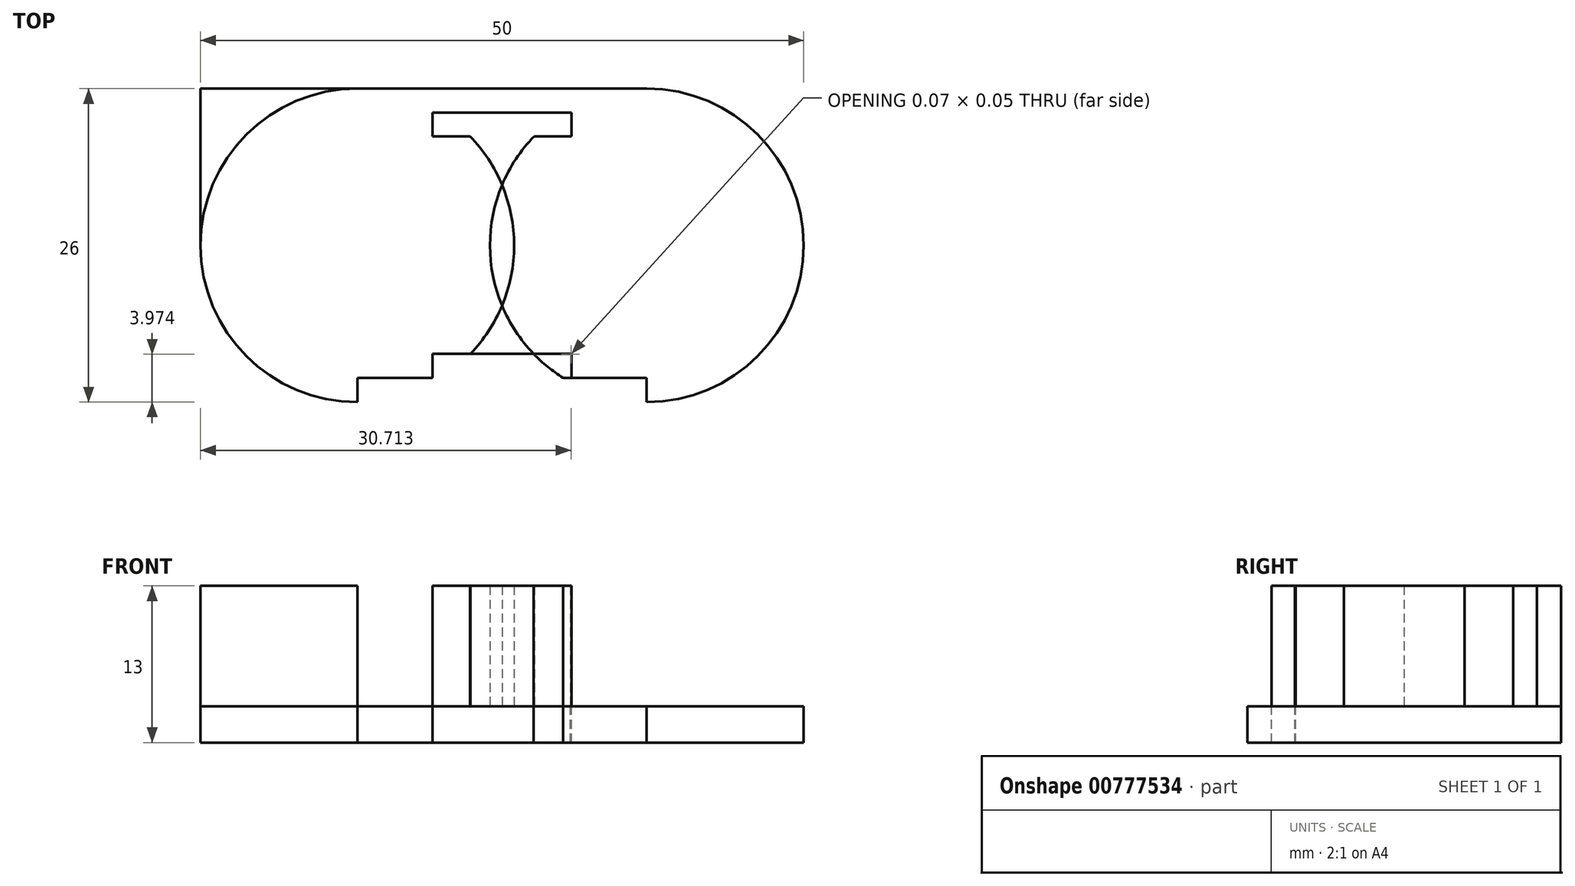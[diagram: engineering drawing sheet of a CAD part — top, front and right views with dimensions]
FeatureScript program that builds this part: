
annotation { "Feature Type Name" : "Feature", "Feature Type Description" : "" }
export const myFeature = defineFeature(function(context is Context, id is Id, definition is map)
    precondition{}
    {
        {
            var Q0;
            Q0=qCreatedBy(makeId("Top.planeOp"),FACE);
            var sketch = newSketch(context, id + "F0", { "sketchPlane" : qUnion([Q0])});
            skLineSegment(sketch, "E0.bottom", {"start": v(0, 26) * mm, "end": v(50, 26) * mm});
            skLineSegment(sketch, "E0.top", {"start": v(0, 0) * mm, "end": v(50, 0) * mm});
            skLineSegment(sketch, "E0.left", {"start": v(0, 26) * mm, "end": v(0, 0) * mm});
            skLineSegment(sketch, "E0.right", {"start": v(50, 26) * mm, "end": v(50, 0) * mm});
            skLineSegment(sketch, "E1", {"start": v(0, 13) * mm, "end": v(13, 13) * mm});
            skLineSegment(sketch, "E2", {"start": v(13, 13) * mm, "end": v(13, 0) * mm});
            skCircle(sketch, "E3", {"center": v(13, 13) * mm, "radius": 13 * mm});
            skLineSegment(sketch, "E4", {"start": v(50, 13) * mm, "end": v(37, 13) * mm});
            skLineSegment(sketch, "E5", {"start": v(37, 13) * mm, "end": v(37, 0) * mm});
            skCircle(sketch, "E6", {"center": v(37, 13) * mm, "radius": 13 * mm});
            skLineSegment(sketch, "E7", {"start": v(0, 0) * mm, "end": v(25, 0) * mm, "construction": true});
            skLineSegment(sketch, "E8.bottom", {"start": v(19.25, 0) * mm, "end": v(30.75, 0) * mm});
            skCircle(sketch, "E9", {"center": v(13, 13) * mm, "radius": 11 * mm});
            skCircle(sketch, "E10", {"center": v(37, 13) * mm, "radius": 11 * mm});
            skLineSegment(sketch, "E11", {"start": v(13, 24) * mm, "end": v(37, 24) * mm});
            skLineSegment(sketch, "E12", {"start": v(13, 13) * mm, "end": v(13, 24) * mm, "construction": true});
            skLineSegment(sketch, "E13", {"start": v(37, 13) * mm, "end": v(37, 24) * mm, "construction": true});
            skLineSegment(sketch, "E14", {"start": v(13, 2) * mm, "end": v(37, 2) * mm});
            skLineSegment(sketch, "E15.bottom", {"start": v(19.25, 2) * mm, "end": v(30.75, 2) * mm});
            skLineSegment(sketch, "E15.top", {"start": v(19.25, 4) * mm, "end": v(30.75, 4) * mm});
            skLineSegment(sketch, "E15.left", {"start": v(19.25, 2) * mm, "end": v(19.25, 4) * mm});
            skLineSegment(sketch, "E15.right", {"start": v(30.75, 2) * mm, "end": v(30.75, 4) * mm});
            skLineSegment(sketch, "E16", {"start": v(30.75, 0) * mm, "end": v(30.75, 2) * mm, "construction": true});
            skLineSegment(sketch, "E17.top", {"start": v(19.25, 24) * mm, "end": v(30.75, 24) * mm});
            skLineSegment(sketch, "E17.left", {"start": v(19.25, 2) * mm, "end": v(19.25, 24) * mm, "construction": true});
            skLineSegment(sketch, "E17.right", {"start": v(30.75, 2) * mm, "end": v(30.75, 24) * mm, "construction": true});
            skLineSegment(sketch, "E18.bottom", {"start": v(19.25, 24) * mm, "end": v(30.75, 24) * mm, "construction": true});
            skLineSegment(sketch, "E18.top", {"start": v(19.25, 22.05) * mm, "end": v(30.75, 22.05) * mm});
            skLineSegment(sketch, "E18.left", {"start": v(19.25, 24) * mm, "end": v(19.25, 22.05) * mm});
            skLineSegment(sketch, "E18.right", {"start": v(30.75, 24) * mm, "end": v(30.75, 22.05) * mm});
            skSolve(sketch);
        }
        {
            var Q0;
            {var subQ0=sQuery(id+"F0.wireOp",EDGE,"E18.top");var subQ1=sQuery(id+"F0.wireOp",EDGE,"E3");var subQ2=makeQuery(id+"F0.imprint","INTERSECT",VERTEX,{"derivedFrom":[subQ1,subQ0]});Q0=makeQuery(id+"F0.imprint","IMPRINT",FACE,{"disambiguationData":[TD([[makeQuery(id+"F0.imprint","IMPRINT",EDGE,{"disambiguationData":[TD([[subQ2,-1.0]])],"derivedFrom":subQ1}),-1.0]])]});}
            var Q1;
            {var subQ5=sQuery(id+"F0.wireOp",EDGE,"E18.left");Q1=makeQuery(id+"F0.imprint","IMPRINT",FACE,{"disambiguationData":[TD([[makeQuery(id+"F0.imprint","IMPRINT",EDGE,{"derivedFrom":subQ5}),1.0]])]});}
            var Q2;
            {var subQ5=sQuery(id+"F0.wireOp",EDGE,"E18.right");Q2=makeQuery(id+"F0.imprint","IMPRINT",FACE,{"disambiguationData":[TD([[makeQuery(id+"F0.imprint","IMPRINT",EDGE,{"derivedFrom":subQ5}),-1.0]])]});}
            var Q3;
            {var subQ0=sQuery(id+"F0.wireOp",EDGE,"E15.bottom");var subQ1=sQuery(id+"F0.wireOp",EDGE,"E3");var subQ2=makeQuery(id+"F0.imprint","INTERSECT",VERTEX,{"derivedFrom":[subQ1,subQ0]});Q3=makeQuery(id+"F0.imprint","IMPRINT",FACE,{"disambiguationData":[TD([[makeQuery(id+"F0.imprint","IMPRINT",EDGE,{"disambiguationData":[TD([[subQ2,-1.0]])],"derivedFrom":subQ1}),-1.0]])]});}
            var Q4;
            {var subQ0=sQuery(id+"F0.wireOp",EDGE,"E15.bottom");var subQ6=sQuery(id+"F0.wireOp",EDGE,"E3");var subQ9=makeQuery(id+"F0.imprint","INTERSECT",VERTEX,{"derivedFrom":[subQ6,subQ0]});Q4=makeQuery(id+"F0.imprint","IMPRINT",FACE,{"disambiguationData":[TD([[makeQuery(id+"F0.imprint","IMPRINT",EDGE,{"disambiguationData":[TD([[subQ9,-1.0]])],"derivedFrom":subQ6}),1.0]])]});}
            var Q5;
            {var subQ5=sQuery(id+"F0.wireOp",EDGE,"E15.top");var subQ6=sQuery(id+"F0.wireOp",EDGE,"E6");var subQ7=makeQuery(id+"F0.imprint","INTERSECT",VERTEX,{"derivedFrom":[subQ6,subQ5]});Q5=makeQuery(id+"F0.imprint","IMPRINT",FACE,{"disambiguationData":[TD([[makeQuery(id+"F0.imprint","IMPRINT",EDGE,{"disambiguationData":[TD([[subQ7,-1.0]])],"derivedFrom":subQ6}),1.0]])]});}
            extrude(context, id + "F1", {"entities" : qUnion([Q0, Q1, Q2, Q3, Q4, Q5]), "depth" : 10 * mm, "offsetDistance" : 25 * mm});
        }
        {
            var Q0;
            {var subQ1=sQuery(id+"F0.wireOp",EDGE,"E4");var subQ3=sQuery(id+"F0.wireOp",EDGE,"E10");var subQ4=makeQuery(id+"F0.imprint","INTERSECT",VERTEX,{"derivedFrom":[subQ1,subQ3]});Q0=makeQuery(id+"F0.imprint","IMPRINT",FACE,{"disambiguationData":[TD([[makeQuery(id+"F0.imprint","IMPRINT",EDGE,{"disambiguationData":[TD([[subQ4,1.0]])],"derivedFrom":subQ1}),1.0]])]});}
            var Q1;
            {var subQ5=sQuery(id+"F0.wireOp",EDGE,"E6");var subQ7=makeQuery(id+"F0.imprint","INTERSECT",VERTEX,{"derivedFrom":[sQuery(id+"F0.wireOp",EDGE,"E0.bottom"),subQ5]});Q1=makeQuery(id+"F0.imprint","IMPRINT",FACE,{"disambiguationData":[TD([[makeQuery(id+"F0.imprint","IMPRINT",EDGE,{"disambiguationData":[TD([[subQ7,-1.0]])],"derivedFrom":subQ5}),1.0]])]});}
            var Q2;
            {var subQ3=sQuery(id+"F0.wireOp",EDGE,"E5");var subQ4=sQuery(id+"F0.wireOp",EDGE,"E4");var subQ5=makeQuery(id+"F0.imprint","INTERSECT",VERTEX,{"derivedFrom":[subQ4,subQ3]});Q2=makeQuery(id+"F0.imprint","IMPRINT",FACE,{"disambiguationData":[TD([[makeQuery(id+"F0.imprint","IMPRINT",EDGE,{"disambiguationData":[TD([[subQ5,1.0]])],"derivedFrom":subQ4}),-1.0]])]});}
            var Q3;
            {var subQ3=sQuery(id+"F0.wireOp",EDGE,"E18.right");Q3=makeQuery(id+"F0.imprint","IMPRINT",FACE,{"disambiguationData":[TD([[makeQuery(id+"F0.imprint","IMPRINT",EDGE,{"derivedFrom":subQ3}),1.0]])]});}
            var Q4;
            {var subQ5=sQuery(id+"F0.wireOp",EDGE,"E18.right");Q4=makeQuery(id+"F0.imprint","IMPRINT",FACE,{"disambiguationData":[TD([[makeQuery(id+"F0.imprint","IMPRINT",EDGE,{"derivedFrom":subQ5}),-1.0]])]});}
            var Q5;
            {var subQ0=sQuery(id+"F0.wireOp",EDGE,"E6");var subQ1=sQuery(id+"F0.wireOp",EDGE,"E3");var subQ2=makeQuery(id+"F0.imprint","INTERSECT",VERTEX,{"disambiguationData":[OD(0.0)],"derivedFrom":[subQ1,subQ0]});Q5=makeQuery(id+"F0.imprint","IMPRINT",FACE,{"disambiguationData":[TD([[makeQuery(id+"F0.imprint","IMPRINT",EDGE,{"disambiguationData":[TD([[subQ2,1.0]])],"derivedFrom":subQ1}),1.0]])]});}
            var Q6;
            {var subQ0=sQuery(id+"F0.wireOp",EDGE,"E10");var subQ1=sQuery(id+"F0.wireOp",EDGE,"E3");var subQ2=makeQuery(id+"F0.imprint","INTERSECT",VERTEX,{"derivedFrom":[subQ1,subQ0]});Q6=makeQuery(id+"F0.imprint","IMPRINT",FACE,{"disambiguationData":[TD([[makeQuery(id+"F0.imprint","IMPRINT",EDGE,{"disambiguationData":[TD([[subQ2,1.0]])],"derivedFrom":subQ1}),-1.0]])]});}
            var Q7;
            {var subQ5=sQuery(id+"F0.wireOp",EDGE,"E15.top");var subQ6=sQuery(id+"F0.wireOp",EDGE,"E6");var subQ7=makeQuery(id+"F0.imprint","INTERSECT",VERTEX,{"derivedFrom":[subQ6,subQ5]});Q7=makeQuery(id+"F0.imprint","IMPRINT",FACE,{"disambiguationData":[TD([[makeQuery(id+"F0.imprint","IMPRINT",EDGE,{"disambiguationData":[TD([[subQ7,-1.0]])],"derivedFrom":subQ6}),1.0]])]});}
            var Q8;
            {var subQ1=sQuery(id+"F0.wireOp",EDGE,"E10");var subQ3=sQuery(id+"F0.wireOp",EDGE,"E15.right");var subQ4=makeQuery(id+"F0.imprint","INTERSECT",VERTEX,{"derivedFrom":[subQ1,subQ3]});Q8=makeQuery(id+"F0.imprint","IMPRINT",FACE,{"disambiguationData":[TD([[makeQuery(id+"F0.imprint","IMPRINT",EDGE,{"disambiguationData":[TD([[subQ4,-1.0]])],"derivedFrom":subQ1}),-1.0]])]});}
            var Q9;
            {var subQ0=sQuery(id+"F0.wireOp",EDGE,"E6");var subQ5=sQuery(id+"F0.wireOp",EDGE,"E15.bottom");var subQ6=makeQuery(id+"F0.imprint","INTERSECT",VERTEX,{"derivedFrom":[subQ0,subQ5]});Q9=makeQuery(id+"F0.imprint","IMPRINT",FACE,{"disambiguationData":[TD([[makeQuery(id+"F0.imprint","IMPRINT",EDGE,{"disambiguationData":[TD([[subQ6,-1.0]])],"derivedFrom":subQ0}),1.0]])]});}
            var Q10;
            {var subQ0=sQuery(id+"F0.wireOp",EDGE,"E6");var subQ1=sQuery(id+"F0.wireOp",EDGE,"E3");var subQ2=makeQuery(id+"F0.imprint","INTERSECT",VERTEX,{"disambiguationData":[OD(0.0)],"derivedFrom":[subQ1,subQ0]});Q10=makeQuery(id+"F0.imprint","IMPRINT",FACE,{"disambiguationData":[TD([[makeQuery(id+"F0.imprint","IMPRINT",EDGE,{"disambiguationData":[TD([[subQ2,1.0]])],"derivedFrom":subQ1}),-1.0]])]});}
            var Q11;
            {var subQ0=sQuery(id+"F0.wireOp",EDGE,"E6");var subQ1=sQuery(id+"F0.wireOp",EDGE,"E3");var subQ2=makeQuery(id+"F0.imprint","INTERSECT",VERTEX,{"disambiguationData":[OD(0.0)],"derivedFrom":[subQ1,subQ0]});Q11=makeQuery(id+"F0.imprint","IMPRINT",FACE,{"disambiguationData":[TD([[makeQuery(id+"F0.imprint","IMPRINT",EDGE,{"disambiguationData":[TD([[subQ2,-1.0]])],"derivedFrom":subQ1}),-1.0]])]});}
            var Q12;
            {var subQ0=sQuery(id+"F0.wireOp",EDGE,"E18.top");var subQ1=sQuery(id+"F0.wireOp",EDGE,"E3");var subQ2=makeQuery(id+"F0.imprint","INTERSECT",VERTEX,{"derivedFrom":[subQ1,subQ0]});Q12=makeQuery(id+"F0.imprint","IMPRINT",FACE,{"disambiguationData":[TD([[makeQuery(id+"F0.imprint","IMPRINT",EDGE,{"disambiguationData":[TD([[subQ2,-1.0]])],"derivedFrom":subQ1}),-1.0]])]});}
            var Q13;
            {var subQ5=sQuery(id+"F0.wireOp",EDGE,"E18.left");Q13=makeQuery(id+"F0.imprint","IMPRINT",FACE,{"disambiguationData":[TD([[makeQuery(id+"F0.imprint","IMPRINT",EDGE,{"derivedFrom":subQ5}),1.0]])]});}
            var Q14;
            {var subQ0=sQuery(id+"F0.wireOp",EDGE,"E6");var subQ1=sQuery(id+"F0.wireOp",EDGE,"E3");var subQ2=makeQuery(id+"F0.imprint","INTERSECT",VERTEX,{"disambiguationData":[OD(0.0)],"derivedFrom":[subQ1,subQ0]});Q14=makeQuery(id+"F0.imprint","IMPRINT",FACE,{"disambiguationData":[TD([[makeQuery(id+"F0.imprint","IMPRINT",EDGE,{"disambiguationData":[TD([[subQ2,-1.0]])],"derivedFrom":subQ1}),1.0]])]});}
            var Q15;
            {var subQ4=sQuery(id+"F0.wireOp",EDGE,"E2");var subQ5=sQuery(id+"F0.wireOp",EDGE,"E1");var subQ6=makeQuery(id+"F0.imprint","INTERSECT",VERTEX,{"derivedFrom":[subQ5,subQ4]});Q15=makeQuery(id+"F0.imprint","IMPRINT",FACE,{"disambiguationData":[TD([[makeQuery(id+"F0.imprint","IMPRINT",EDGE,{"disambiguationData":[TD([[subQ6,1.0]])],"derivedFrom":subQ5}),1.0]])]});}
            var Q16;
            {var subQ0=sQuery(id+"F0.wireOp",EDGE,"E15.top");var subQ1=sQuery(id+"F0.wireOp",EDGE,"E3");var subQ2=makeQuery(id+"F0.imprint","INTERSECT",VERTEX,{"derivedFrom":[subQ1,subQ0]});Q16=makeQuery(id+"F0.imprint","IMPRINT",FACE,{"disambiguationData":[TD([[makeQuery(id+"F0.imprint","IMPRINT",EDGE,{"disambiguationData":[TD([[subQ2,-1.0]])],"derivedFrom":subQ1}),1.0]])]});}
            var Q17;
            {var subQ1=sQuery(id+"F0.wireOp",EDGE,"E9");var subQ3=sQuery(id+"F0.wireOp",EDGE,"E15.left");var subQ4=makeQuery(id+"F0.imprint","INTERSECT",VERTEX,{"derivedFrom":[subQ1,subQ3]});Q17=makeQuery(id+"F0.imprint","IMPRINT",FACE,{"disambiguationData":[TD([[makeQuery(id+"F0.imprint","IMPRINT",EDGE,{"disambiguationData":[TD([[subQ4,1.0]])],"derivedFrom":subQ1}),-1.0]])]});}
            var Q18;
            {var subQ0=sQuery(id+"F0.wireOp",EDGE,"E15.bottom");var subQ6=sQuery(id+"F0.wireOp",EDGE,"E3");var subQ9=makeQuery(id+"F0.imprint","INTERSECT",VERTEX,{"derivedFrom":[subQ6,subQ0]});Q18=makeQuery(id+"F0.imprint","IMPRINT",FACE,{"disambiguationData":[TD([[makeQuery(id+"F0.imprint","IMPRINT",EDGE,{"disambiguationData":[TD([[subQ9,-1.0]])],"derivedFrom":subQ6}),1.0]])]});}
            var Q19;
            {var subQ0=sQuery(id+"F0.wireOp",EDGE,"E15.bottom");var subQ1=sQuery(id+"F0.wireOp",EDGE,"E3");var subQ2=makeQuery(id+"F0.imprint","INTERSECT",VERTEX,{"derivedFrom":[subQ1,subQ0]});Q19=makeQuery(id+"F0.imprint","IMPRINT",FACE,{"disambiguationData":[TD([[makeQuery(id+"F0.imprint","IMPRINT",EDGE,{"disambiguationData":[TD([[subQ2,-1.0]])],"derivedFrom":subQ1}),-1.0]])]});}
            var Q20;
            {var subQ0=sQuery(id+"F0.wireOp",EDGE,"E15.top");var subQ1=sQuery(id+"F0.wireOp",EDGE,"E3");var subQ2=makeQuery(id+"F0.imprint","INTERSECT",VERTEX,{"derivedFrom":[subQ1,subQ0]});Q20=makeQuery(id+"F0.imprint","IMPRINT",FACE,{"disambiguationData":[TD([[makeQuery(id+"F0.imprint","IMPRINT",EDGE,{"disambiguationData":[TD([[subQ2,-1.0]])],"derivedFrom":subQ1}),-1.0]])]});}
            var Q21;
            {var subQ3=sQuery(id+"F0.wireOp",EDGE,"E18.left");Q21=makeQuery(id+"F0.imprint","IMPRINT",FACE,{"disambiguationData":[TD([[makeQuery(id+"F0.imprint","IMPRINT",EDGE,{"derivedFrom":subQ3}),-1.0]])]});}
            var Q22;
            {var subQ5=sQuery(id+"F0.wireOp",EDGE,"E3");var subQ7=makeQuery(id+"F0.imprint","INTERSECT",VERTEX,{"derivedFrom":[sQuery(id+"F0.wireOp",EDGE,"E0.bottom"),subQ5]});Q22=makeQuery(id+"F0.imprint","IMPRINT",FACE,{"disambiguationData":[TD([[makeQuery(id+"F0.imprint","IMPRINT",EDGE,{"disambiguationData":[TD([[subQ7,1.0]])],"derivedFrom":subQ5}),1.0]])]});}
            var Q23;
            {var subQ0=sQuery(id+"F0.wireOp",EDGE,"E2");var subQ1=sQuery(id+"F0.wireOp",EDGE,"E1");var subQ2=makeQuery(id+"F0.imprint","INTERSECT",VERTEX,{"derivedFrom":[subQ1,subQ0]});Q23=makeQuery(id+"F0.imprint","IMPRINT",FACE,{"disambiguationData":[TD([[makeQuery(id+"F0.imprint","IMPRINT",EDGE,{"disambiguationData":[TD([[subQ2,1.0]])],"derivedFrom":subQ1}),-1.0]])]});}
            var Q24;
            {var subQ1=sQuery(id+"F0.wireOp",EDGE,"E1");var subQ3=sQuery(id+"F0.wireOp",EDGE,"E9");var subQ4=makeQuery(id+"F0.imprint","INTERSECT",VERTEX,{"derivedFrom":[subQ1,subQ3]});Q24=makeQuery(id+"F0.imprint","IMPRINT",FACE,{"disambiguationData":[TD([[makeQuery(id+"F0.imprint","IMPRINT",EDGE,{"disambiguationData":[TD([[subQ4,1.0]])],"derivedFrom":subQ1}),-1.0]])]});}
            var Q25;
            {var subQ0=sQuery(id+"F0.wireOp",EDGE,"E3");var subQ5=sQuery(id+"F0.wireOp",EDGE,"E15.bottom");var subQ6=makeQuery(id+"F0.imprint","INTERSECT",VERTEX,{"derivedFrom":[subQ0,subQ5]});Q25=makeQuery(id+"F0.imprint","IMPRINT",FACE,{"disambiguationData":[TD([[makeQuery(id+"F0.imprint","IMPRINT",EDGE,{"disambiguationData":[TD([[subQ6,1.0]])],"derivedFrom":subQ0}),1.0]])]});}
            var Q26;
            {var subQ7=sQuery(id+"F0.wireOp",EDGE,"E8.bottom");Q26=makeQuery(id+"F0.imprint","IMPRINT",FACE,{"disambiguationData":[TD([[makeQuery(id+"F0.imprint","IMPRINT",EDGE,{"derivedFrom":subQ7}),1.0]])]});}
            var Q27;
            {var subQ0=sQuery(id+"F0.wireOp",EDGE,"E3");var subQ1=sQuery(id+"F0.wireOp",EDGE,"E0.bottom");var subQ2=makeQuery(id+"F0.imprint","INTERSECT",VERTEX,{"derivedFrom":[subQ1,subQ0]});Q27=makeQuery(id+"F0.imprint","IMPRINT",FACE,{"disambiguationData":[TD([[makeQuery(id+"F0.imprint","IMPRINT",EDGE,{"disambiguationData":[TD([[subQ2,-1.0]])],"derivedFrom":subQ1}),-1.0]])]});}
            var Q28;
            {var subQ0=sQuery(id+"F0.wireOp",EDGE,"E5");var subQ1=sQuery(id+"F0.wireOp",EDGE,"E4");var subQ2=makeQuery(id+"F0.imprint","INTERSECT",VERTEX,{"derivedFrom":[subQ1,subQ0]});Q28=makeQuery(id+"F0.imprint","IMPRINT",FACE,{"disambiguationData":[TD([[makeQuery(id+"F0.imprint","IMPRINT",EDGE,{"disambiguationData":[TD([[subQ2,1.0]])],"derivedFrom":subQ1}),1.0]])]});}
            extrude(context, id + "F2", {"entities" : qUnion([Q0, Q1, Q2, Q3, Q4, Q5, Q6, Q7, Q8, Q9, Q10, Q11, Q12, Q13, Q14, Q15, Q16, Q17, Q18, Q19, Q20, Q21, Q22, Q23, Q24, Q25, Q26, Q27, Q28]), "oppositeDirection" : true, "depth" : 3 * mm, "offsetDistance" : 25 * mm});
        }
    });
